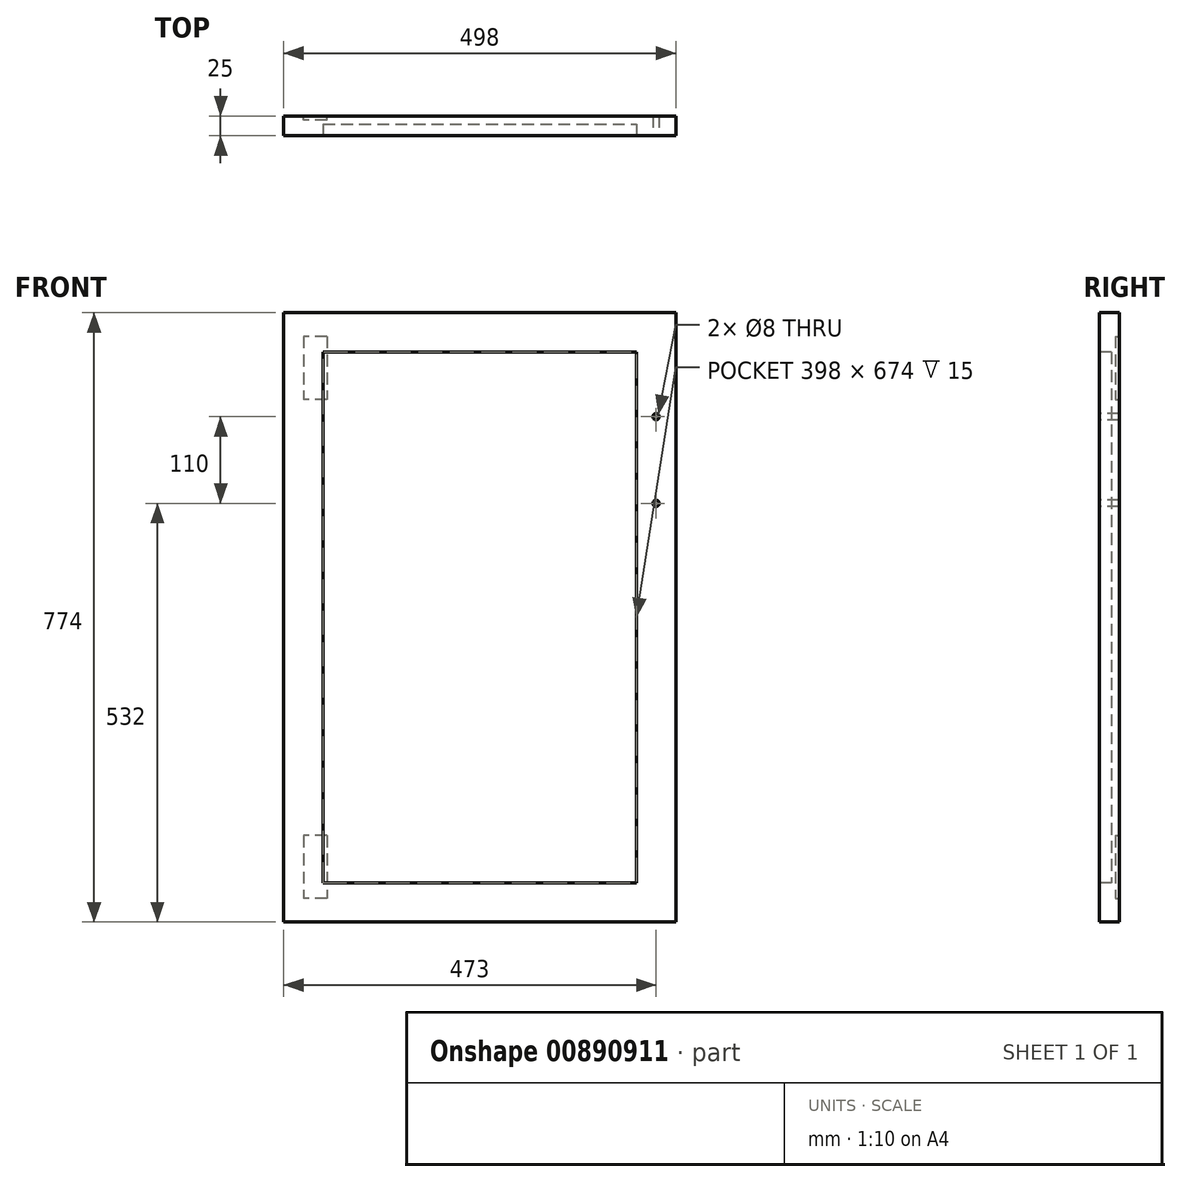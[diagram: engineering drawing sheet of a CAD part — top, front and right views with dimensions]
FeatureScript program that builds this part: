
annotation { "Feature Type Name" : "Feature", "Feature Type Description" : "" }
export const myFeature = defineFeature(function(context is Context, id is Id, definition is map)
    precondition{}
    {
        {
            var Q0;
            Q0=qCreatedBy(makeId("Front.planeOp"),FACE);
            var sketch = newSketch(context, id + "F0", { "sketchPlane" : qUnion([Q0])});
            skLineSegment(sketch, "E0.bottom", {"start": v(249, 387) * mm, "end": v(-249, 387) * mm});
            skLineSegment(sketch, "E0.top", {"start": v(249, -387) * mm, "end": v(-249, -387) * mm});
            skLineSegment(sketch, "E0.left", {"start": v(249, 387) * mm, "end": v(249, -387) * mm});
            skLineSegment(sketch, "E0.right", {"start": v(-249, 387) * mm, "end": v(-249, -387) * mm});
            skPoint(sketch, "E0.middle", {"position": v(0, 0) * mm});
            skSolve(sketch);
        }
        {
            var Q0;
            Q0 = qSketchRegion(id + "F0", true);
            extrude(context, id + "F1", {"entities" : qUnion([Q0]), "depth" : 25 * mm, "offsetDistance" : 25 * mm});
        }
        {
            var Q0;
            Q0=makeQuery(id+"F1.opExtrude","CAP_FACE",FACE,{"disambiguationData":[OSD([sQuery(id+"F0.wireOp",EDGE,"E0.bottom"),sQuery(id+"F0.wireOp",EDGE,"E0.top"),sQuery(id+"F0.wireOp",EDGE,"E0.left"),sQuery(id+"F0.wireOp",EDGE,"E0.right")])],"isStart":false});
            var sketch = newSketch(context, id + "F2", { "sketchPlane" : qUnion([Q0])});
            skLineSegment(sketch, "E1.bottom", {"start": v(-199, 337) * mm, "end": v(199, 337) * mm});
            skLineSegment(sketch, "E1.top", {"start": v(-199, -337) * mm, "end": v(199, -337) * mm});
            skLineSegment(sketch, "E1.left", {"start": v(-199, 337) * mm, "end": v(-199, -337) * mm});
            skLineSegment(sketch, "E1.right", {"start": v(199, 337) * mm, "end": v(199, -337) * mm});
            skPoint(sketch, "E1.middle", {"position": v(0, 0) * mm});
            skSolve(sketch);
        }
        {
            var Q0;
            Q0 = qSketchRegion(id + "F2", true);
            extrude(context, id + "F3", {"entities" : qUnion([Q0]), "operationType" : NewBodyOperationType.REMOVE, "oppositeDirection" : true, "depth" : 15 * mm, "offsetDistance" : 25 * mm});
        }
        {
            var Q0;
            Q0=makeQuery(id+"F1.opExtrude","CAP_FACE",FACE,{"disambiguationData":[OSD([sQuery(id+"F0.wireOp",EDGE,"E0.bottom"),sQuery(id+"F0.wireOp",EDGE,"E0.top"),sQuery(id+"F0.wireOp",EDGE,"E0.left"),sQuery(id+"F0.wireOp",EDGE,"E0.right")])],"isStart":false});
            var sketch = newSketch(context, id + "F4", { "sketchPlane" : qUnion([Q0])});
            skLineSegment(sketch, "E2", {"start": v(199, 0) * mm, "end": v(249, 0) * mm, "construction": true});
            skLineSegment(sketch, "E3", {"start": v(224, 200) * mm, "end": v(224, 255) * mm});
            skLineSegment(sketch, "E4", {"start": v(224, 200) * mm, "end": v(224, 145) * mm});
            skLineSegment(sketch, "E5", {"start": v(224, 0) * mm, "end": v(224, 200) * mm, "construction": true});
            skCircle(sketch, "E6", {"center": v(224, 145) * mm, "radius": 4 * mm});
            skCircle(sketch, "E7", {"center": v(224, 255) * mm, "radius": 4 * mm});
            skSolve(sketch);
        }
        {
            var Q0;
            Q0 = qSketchRegion(id + "F4", true);
            extrude(context, id + "F5", {"entities" : qUnion([Q0]), "operationType" : NewBodyOperationType.REMOVE, "endBound" : BoundingType.UP_TO_NEXT, "oppositeDirection" : true, "depth" : 25 * mm, "offsetDistance" : 25 * mm});
        }
        {
            var Q0;
            Q0=makeQuery(id+"F1.opExtrude","CAP_FACE",FACE,{"disambiguationData":[OSD([sQuery(id+"F0.wireOp",EDGE,"E0.bottom"),sQuery(id+"F0.wireOp",EDGE,"E0.top"),sQuery(id+"F0.wireOp",EDGE,"E0.left"),sQuery(id+"F0.wireOp",EDGE,"E0.right")])],"isStart":true});
            var sketch = newSketch(context, id + "F6", { "sketchPlane" : qUnion([Q0])});
            skLineSegment(sketch, "E8.bottom", {"start": v(194, 357) * mm, "end": v(224, 357) * mm});
            skLineSegment(sketch, "E8.top", {"start": v(194, 277) * mm, "end": v(224, 277) * mm});
            skLineSegment(sketch, "E8.left", {"start": v(194, 357) * mm, "end": v(194, 277) * mm});
            skLineSegment(sketch, "E8.right", {"start": v(224, 357) * mm, "end": v(224, 277) * mm});
            skLineSegment(sketch, "E9.bottom", {"start": v(194, -277) * mm, "end": v(224, -277) * mm});
            skLineSegment(sketch, "E9.top", {"start": v(194, -357) * mm, "end": v(224, -357) * mm});
            skLineSegment(sketch, "E9.left", {"start": v(224, -277) * mm, "end": v(224, -357) * mm});
            skLineSegment(sketch, "E9.right", {"start": v(194, -277) * mm, "end": v(194, -357) * mm});
            skSolve(sketch);
        }
        {
            var Q0;
            Q0 = qSketchRegion(id + "F6", true);
            extrude(context, id + "F7", {"entities" : qUnion([Q0]), "operationType" : NewBodyOperationType.REMOVE, "oppositeDirection" : true, "depth" : 5 * mm, "offsetDistance" : 25 * mm});
        }
    });
